# Revit family: IS_iLifeB_T5285_BIM_NL
name_source: partatom
category: Plumbing Fixtures
units: mm (PartAtom-declared; Revit-internal decimal feet)

## family parameters
Always vertical = No
Cut with Voids When Loaded = No
OmniClass Number = 23.45.05.14.21.11
OmniClass Title = Bath/Shower Units
Part Type = Normal
Room Calculation Point = No
Round Connector Dimension = Use Diameter
Shared = No
Work Plane-Based = No

## types (7) — shared parameters
Accessories = https://www.idealstandard.co.uk
Afmetingen = https://www.idealstandard.nl
AfstandsEenheid = Millimeter
AreaUnits = millimetres
AssetType = Fixed
Auteur = Ideal Standard
BIMObjectName = IS_IdealStandard_BathroomCabinets_I.LifeB_T5268
BIMobject category = Storage
BIMobject category code = sanitary-storage
BIMobject main category = Sanitary
BIMobject main category code = sanitary
Beschrijvinggarantie = Herstellergarantie
BimObjectNaam = IS_IdealStandard_BathroomCabinets_I.LifeB_T5268
Brand = Ideal Standard
Brand url = https://www.idealstandard.nl
Breedte = 1603
Category = Sanitary
Classification = Furniture
CodePerformance = n /a
ComponentNames = n /a
ConnectionType = n /a
Constituents = n /a
CurrencyUnit = €
CurrentRevision = 1
Date of publishing = 09/09/2022
Diepte = 507 mm  [stored 1.66339 ft]
DurationUnit = Years
DuurEenheid = Jahre
Edition number = 1
ElementType = Fixed
Garantieonderdelen = 2
Garantieunits = Jahre
GemaaktOp = 09/09/2022
Help = https://www.idealstandard.nl
Hoogte = 18
Hulp = https://www.idealstandard.nl
IFC Classification = Furniture
IfcExportAs = IfcFurnitureType
IfcExportType = BATHROOMCABINET
Installatieinstructies = https://www.idealstandard.nl
Installation instructions = https://www.idealstandard.nl
InstallationInstructions = https://www.idealstandard.nl
Lengte = 507 mm  [stored 1.66339 ft]
LinearUnits = Millimeter
MaintenanceInformation = https://www.idealstandard.nl
Manufacturer = Ideal Standard
Manufacturer name = Ideal Standard
ManufacturerURL = https://www.idealstandard.nl
Masterformat 2014 Code = 22 40 00
Masterformat 2014 Description = Plumbing Fixtures
Materiaal = Holz
Material = Wood
Material main = Wood
Merk = Ideal Standard
NBS Reference Code = 45-35-72/318
NBS Reference Description = Bathroom cabinets
Name = BathroomCabinets_I.LifeB_T5268_IdealStandard
NettWeight = 9.30 Kg
NominalDepth = 507 mm  [stored 1.66339 ft]
NominalHeight = 18 mm  [stored 0.0590551 ft]
NominalWidth = 1603 mm  [stored 5.25919 ft]
OmniClass Code = 23.45.00.00
OmniClass Description = Sanitary Equipment
OppervlakteEenheid = Millimeter
PredefinedType = Sanitay Furniture
Product Guid = 7ca817ba-8fd3-4f22-9ce1-74ca873693db
Product SKU = T5285
Product certification = https://www.idealstandard.nl
Product data url = https://bimobject.com
Product family = I.life B
Product group = Bathroom Furniture
Product name = I.LIFE B WORKTOP MLTI NO CUT 160CM
Product url = https://www.idealstandard.nl
ProductInformation = https://www.idealstandard.nl
Productinformatie = https://www.idealstandard.nl
QR code = http://bimobject.com
Revisie = 1
Shape = Rectangulard
Size = 1603 x 507 x 18 mm
Space = Internal
SpareParts = https://www.idealstandard.nl
Technical description = https://www.idealstandard.nl
Telefoonnummer = 077 355 08 08
Type Comments = Plumbing
UNSPSC Code = 30181500
URL = https://www.idealstandard.nl
Uniclass 1.4 Code = L8241
Uniclass 1.4 Description = Bathroom cabinets
Uniclass 2.0 Code = Pr_40_30_78_06
Uniclass 2.0 Description = Bathroom Cabinets
Uniclass 2015 Code = Pr_40_30_87_03
Uniclass 2015 Name = Bathroom cabinets
Uniclass2015Beschrijving = Bathroom cabinets
Uniclass2015Code = Pr_40_30_87_03
Uniclass2015Referentie = Pr_40_30_87_03
Uniclass2015Title = Bathroom cabinets
Uniclass2015Version = v1.27
Uniformat II Code = E 2020
Uniformat II Description = Movable Furnishings
Urlproducent = https://www.idealstandard.nl
ValutaEenheid = Euro
Versie = 1
Version = 1
VolumeUnits = Litres
Volumeunits = Liter
Vorm = rechteckig
WRASURL = https://www.wrasapprovals.co.uk
WaarborgGarantieInstallatie = n /a
WarrantyDescription = manufacturer warranty
WarrantyDurationParts = 1
WarrantyDurationUnit = years
Weight Net (Kg) = 9.3
Wisselstukken = https://www.idealstandard.nl
Youtube clip = https://www.youtube.com
zero-valued in all types: BrutoGewicht, Nettogewicht, Vervangingskosten

## per-type parameters (varying)
| type | Afwerking | Artikelnummer | Artikelomschrijving | Artikelreferentie | BarCode | Barcode | Color | Description | Features | Finish | GTIN code | Kleur | MainColor | Model | ModelNumber | ModelReference |
| T5285DU - I.LIFE B WORKTOP MLTI NO CUT 160CM - WHITE MATT | weiß matt | T5285DU | I.LIFE B ARBEITSPLATTE MLTI OHNE SCHNITT 160CM | I.LIFE B ARBEITSPLATTE MLTI OHNE SCHNITT 160CM | 8014140502753 | 8014140502753 | weiß matt | I.LIFE B WORKTOP MLTI NO CUT 160CM | WORKTOP MLTI NO CUT 160CM | white matt | 8014140502753 | weiß matt | weiß matt | T5285DU | T5285DU | I.LIFE B WORKTOP MLTI NO CUT 160CM |
| T5285NF - I.LIFE B WORKTOP SUITEABLE FOR MULTIPLE UNITS NO CUT 160 - SAND BEIGE MATT | sandbeige matt | T5285NF | I.LIFE B ARBEITSPLATTE FÜR MEHRERE EINHEITEN GEEIGNET NO CUT 160 | I.LIFE B ARBEITSPLATTE FÜR MEHRERE EINHEITEN GEEIGNET NO CUT 160 | 8014140494928 | 8014140494928 | sandbeige matt | I.LIFE B WORKTOP SUITEABLE FOR MULTIPLE UNITS NO CUT 160 | WORKTOP SUITEABLE FOR MULTIPLE UNITS NO CUT 160 | sand beige matt | 8014140494928 | sandbeige matt | sandbeige matt | T5285NF | T5285NF | I.LIFE B WORKTOP SUITEABLE FOR MULTIPLE UNITS NO CUT 160 |
| T5285NG - I.LIFE B WORKTOP SUITEABLE FOR MULTIPLE UNITS NO CUT 160 - QUARTZ GREY MATT | quarzgrau matt | T5285NG | I.LIFE B ARBEITSPLATTE FÜR MEHRERE EINHEITEN GEEIGNET NO CUT 160 | I.LIFE B ARBEITSPLATTE FÜR MEHRERE EINHEITEN GEEIGNET NO CUT 160 | 8014140494935 | 8014140494935 | quarzgrau matt | I.LIFE B WORKTOP SUITEABLE FOR MULTIPLE UNITS NO CUT 160 | WORKTOP SUITEABLE FOR MULTIPLE UNITS NO CUT 160 | quartz grey matt | 8014140494935 | quarzgrau matt | quarzgrau matt | T5285NG | T5285NG | I.LIFE B WORKTOP SUITEABLE FOR MULTIPLE UNITS NO CUT 160 |
| T5285NV - I.LIFE B WORKTOP SUITEABLE FOR MULTIPLE UNITS NO CUT 160 - CARBON GREY MATT | carbongrau matt | T5285NV | I.LIFE B ARBEITSPLATTE FÜR MEHRERE EINHEITEN GEEIGNET NO CUT 160 | I.LIFE B ARBEITSPLATTE FÜR MEHRERE EINHEITEN GEEIGNET NO CUT 160 | 8014140494959 | 8014140494959 | carbongrau matt | I.LIFE B WORKTOP SUITEABLE FOR MULTIPLE UNITS NO CUT 160 | WORKTOP SUITEABLE FOR MULTIPLE UNITS NO CUT 160 | carbon grey matt | 8014140494959 | carbongrau matt | carbongrau matt | T5285NV | T5285NV | I.LIFE B WORKTOP SUITEABLE FOR MULTIPLE UNITS NO CUT 160 |
| T5285NH - I.LIFE B WORKTOP SUITEABLE FOR MULTIPLE UNITS NO CUT 160 - GREIGE MATT | grau matt | T5285NH | I.LIFE B ARBEITSPLATTE FÜR MEHRERE EINHEITEN GEEIGNET NO CUT 160 | I.LIFE B ARBEITSPLATTE FÜR MEHRERE EINHEITEN GEEIGNET NO CUT 160 | 8014140494942 | 8014140494942 | grau matt | I.LIFE B WORKTOP SUITEABLE FOR MULTIPLE UNITS NO CUT 160 | WORKTOP SUITEABLE FOR MULTIPLE UNITS NO CUT 160 | greige matt | 8014140494942 | grau matt | grau matt | T5285NH | T5285NH | I.LIFE B WORKTOP SUITEABLE FOR MULTIPLE UNITS NO CUT 160 |
| T5285NX - I.LIFE B WORKTOP MLTI NO CUT 160CM - NATURAL OAK | natürliche Eiche | T5285NX | I.LIFE B ARBEITSPLATTE MLTI OHNE SCHNITT 160CM | I.LIFE B ARBEITSPLATTE MLTI OHNE SCHNITT 160CM | 8014140502777 | 8014140502777 | natürliche Eiche | I.LIFE B WORKTOP MLTI NO CUT 160CM | WORKTOP MLTI NO CUT 160CM | natural oak | 8014140502777 | natürliche Eiche | natürliche Eiche | T5285NX | T5285NX | I.LIFE B WORKTOP MLTI NO CUT 160CM |
| T5285NW - I.LIFE B WORKTOP MLTI NO CUT 160CM - COFFEE OAK | Kaffee Eiche | T5285NW | I.LIFE B ARBEITSPLATTE MLTI OHNE SCHNITT 160CM | I.LIFE B ARBEITSPLATTE MLTI OHNE SCHNITT 160CM | 8014140502760 | 8014140502760 | Kaffee Eiche | I.LIFE B WORKTOP MLTI NO CUT 160CM | WORKTOP MLTI NO CUT 160CM | coffee oak | 8014140502760 | Kaffee Eiche | Kaffee Eiche | T5285NW | T5285NW | I.LIFE B WORKTOP MLTI NO CUT 160CM |

note: [stored X ft] marks values corroborated as IEEE doubles in the binary element streams (Revit-internal decimal feet)

## geometry (parser evidence)
native form markers: Sweep x2
no freeform markers — native parametric forms only
